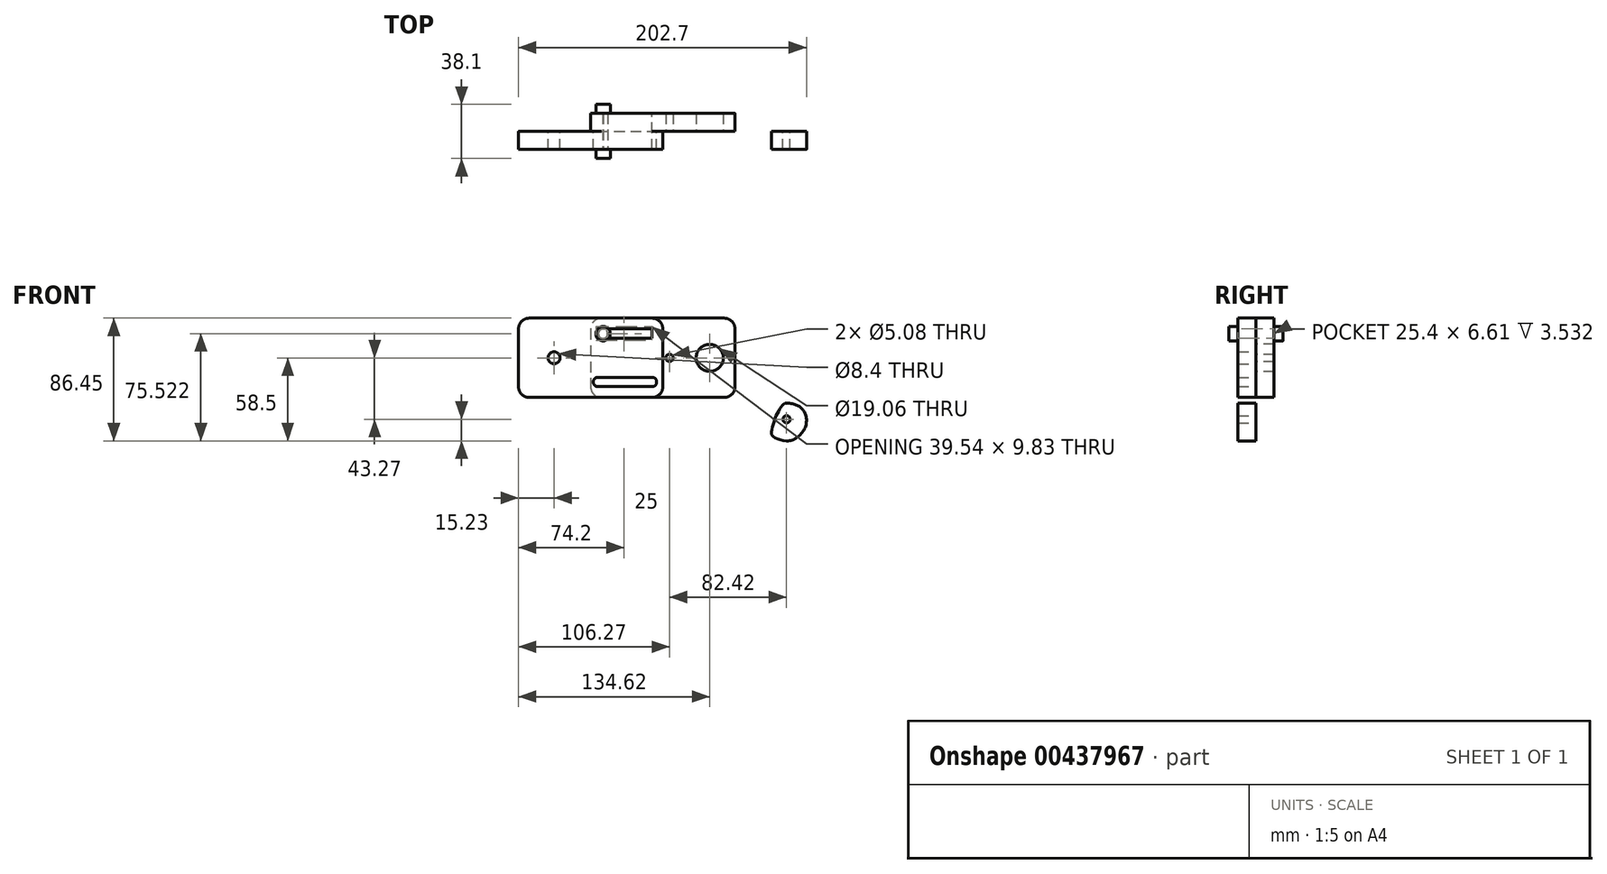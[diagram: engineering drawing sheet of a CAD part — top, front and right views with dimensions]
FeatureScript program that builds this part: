
annotation { "Feature Type Name" : "Feature", "Feature Type Description" : "" }
export const myFeature = defineFeature(function(context is Context, id is Id, definition is map)
    precondition{}
    {
        {
            var Q0;
            Q0=qCreatedBy(makeId("Front.planeOp"),FACE);
            var sketch = newSketch(context, id + "F0", { "sketchPlane" : qUnion([Q0])});
            skLineSegment(sketch, "E0.bottom", {"start": v(-147.55, 96.25) * mm, "end": v(-61.2, 96.25) * mm});
            skLineSegment(sketch, "E0.top", {"start": v(-147.55, 40.37) * mm, "end": v(-61.2, 40.37) * mm});
            skLineSegment(sketch, "E0.left", {"start": v(-155.17, 88.63) * mm, "end": v(-155.17, 47.99) * mm});
            skLineSegment(sketch, "E0.right", {"start": v(-53.57, 88.63) * mm, "end": v(-53.57, 47.99) * mm});
            skCircle(sketch, "E1", {"center": v(-130.17, 68.3) * mm, "radius": 4.2 * mm});
            skPoint(sketch, "E1.centerSnap0", {"position": v(-155.17, 68.3) * mm});
            skLineSegment(sketch, "E2", {"start": v(-99.3, 88.63) * mm, "end": v(-61.2, 88.63) * mm});
            skLineSegment(sketch, "E3", {"start": v(-99.3, 82.02) * mm, "end": v(-61.2, 82.02) * mm});
            skLineSegment(sketch, "E4", {"start": v(-53.57, 68.3) * mm, "end": v(-67.06, 68.3) * mm});
            skArc(sketch, "E5", {"start": v(-99.3, 88.63) * mm, "mid": v(-102.6, 85.32) * mm, "end": v(-99.3, 82.02) * mm});
            skArc(sketch, "E6", {"start": v(-61.2, 82.02) * mm, "mid": v(-57.9, 85.32) * mm, "end": v(-61.2, 88.63) * mm});
            skArc(sketch, "E7.MirrorCS", {"start": v(-99.3, 47.99) * mm, "mid": v(-102.6, 51.29) * mm, "end": v(-99.3, 54.6) * mm});
            skArc(sketch, "E8.MirrorCS", {"start": v(-61.2, 54.6) * mm, "mid": v(-57.9, 51.29) * mm, "end": v(-61.2, 47.99) * mm});
            skLineSegment(sketch, "E9.MirrorCS", {"start": v(-99.3, 54.6) * mm, "end": v(-61.2, 54.6) * mm});
            skLineSegment(sketch, "E10.MirrorCS", {"start": v(-99.3, 47.99) * mm, "end": v(-61.2, 47.99) * mm});
            skPoint(sketch, "E11.visualSharp", {"position": v(-155.17, 96.25) * mm});
            skArc(sketch, "E11.filletArc", {"start": v(-147.55, 96.25) * mm, "mid": v(-152.94, 94.02) * mm, "end": v(-155.17, 88.63) * mm});
            skPoint(sketch, "E12.visualSharp", {"position": v(-155.17, 40.37) * mm});
            skArc(sketch, "E12.filletArc", {"start": v(-155.17, 47.99) * mm, "mid": v(-152.94, 42.6) * mm, "end": v(-147.55, 40.37) * mm});
            skPoint(sketch, "E13.visualSharp", {"position": v(-53.57, 96.25) * mm});
            skArc(sketch, "E13.filletArc", {"start": v(-53.57, 88.63) * mm, "mid": v(-55.8, 94.02) * mm, "end": v(-61.2, 96.25) * mm});
            skPoint(sketch, "E14.visualSharp", {"position": v(-53.57, 40.37) * mm});
            skArc(sketch, "E14.filletArc", {"start": v(-61.2, 40.37) * mm, "mid": v(-55.8, 42.6) * mm, "end": v(-53.57, 47.99) * mm});
            skArc(sketch, "E15", {"start": v(-53.57, 73.39) * mm, "mid": v(-53.99, 68.3) * mm, "end": v(-53.57, 63.23) * mm});
            skCircle(sketch, "E16", {"center": v(-130.17, 68.3) * mm, "radius": 29.6 * mm});
            skLineSegment(sketch, "E17", {"start": v(-99.3, 88.63) * mm, "end": v(-99.3, 82.02) * mm});
            skLineSegment(sketch, "E18", {"start": v(-61.2, 82.02) * mm, "end": v(-61.2, 88.63) * mm});
            skLineSegment(sketch, "E19", {"start": v(-99.3, 54.6) * mm, "end": v(-99.3, 47.99) * mm});
            skLineSegment(sketch, "E20", {"start": v(-61.2, 54.6) * mm, "end": v(-61.2, 47.99) * mm});
            skSolve(sketch);
        }
        {
            var Q0;
            Q0=makeQuery(id+"F0.imprint","IMPRINT",FACE,{"disambiguationData":[TD([[makeQuery(id+"F0.imprint","IMPRINT",EDGE,{"derivedFrom":sQuery(id+"F0.wireOp",EDGE,"E0.left")}),1.0]])]});
            var Q1;
            Q1=makeQuery(id+"F0.imprint","IMPRINT",FACE,{"disambiguationData":[TD([[makeQuery(id+"F0.imprint","IMPRINT",EDGE,{"derivedFrom":sQuery(id+"F0.wireOp",EDGE,"E2")}),1.0]])]});
            var Q2;
            Q2=makeQuery(id+"F0.imprint","IMPRINT",FACE,{"disambiguationData":[TD([[makeQuery(id+"F0.imprint","IMPRINT",EDGE,{"derivedFrom":sQuery(id+"F0.wireOp",EDGE,"E1")}),-1.0]])]});
            var Q3;
            Q3=makeQuery(id+"F0.imprint","IMPRINT",FACE,{"disambiguationData":[TD([[makeQuery(id+"F0.imprint","IMPRINT",EDGE,{"derivedFrom":sQuery(id+"F0.wireOp",EDGE,"E1")}),-1.0]])]});
            var Q4;
            Q4=makeQuery(id+"F0.imprint","IMPRINT",FACE,{"disambiguationData":[TD([[makeQuery(id+"F0.imprint","IMPRINT",EDGE,{"derivedFrom":sQuery(id+"F0.wireOp",EDGE,"E6")}),1.0]])]});
            var Q5;
            Q5=makeQuery(id+"F0.imprint","IMPRINT",FACE,{"disambiguationData":[TD([[makeQuery(id+"F0.imprint","IMPRINT",EDGE,{"derivedFrom":sQuery(id+"F0.wireOp",EDGE,"E5")}),1.0]])]});
            var Q6;
            Q6=makeQuery(id+"F0.imprint","IMPRINT",FACE,{"disambiguationData":[TD([[makeQuery(id+"F0.imprint","IMPRINT",EDGE,{"derivedFrom":sQuery(id+"F0.wireOp",EDGE,"E7.MirrorCS")}),-1.0]])]});
            var Q7;
            Q7=makeQuery(id+"F0.imprint","IMPRINT",FACE,{"disambiguationData":[TD([[makeQuery(id+"F0.imprint","IMPRINT",EDGE,{"derivedFrom":sQuery(id+"F0.wireOp",EDGE,"E8.MirrorCS")}),-1.0]])]});
            var Q8;
            {var subQ0=sQuery(id+"F0.wireOp",EDGE,"E4");var subQ1=sQuery(id+"F0.wireOp",EDGE,"E0.right");var subQ2=makeQuery(id+"F0.imprint","INTERSECT",VERTEX,{"derivedFrom":[subQ1,subQ0]});Q8=makeQuery(id+"F0.imprint","IMPRINT",FACE,{"disambiguationData":[TD([[makeQuery(id+"F0.imprint","IMPRINT",EDGE,{"disambiguationData":[TD([[subQ2,-1.0]])],"derivedFrom":subQ1}),-1.0]])]});}
            var Q9;
            {var subQ0=sQuery(id+"F0.wireOp",EDGE,"E4");var subQ1=sQuery(id+"F0.wireOp",EDGE,"E0.right");var subQ2=makeQuery(id+"F0.imprint","INTERSECT",VERTEX,{"derivedFrom":[subQ1,subQ0]});Q9=makeQuery(id+"F0.imprint","IMPRINT",FACE,{"disambiguationData":[TD([[makeQuery(id+"F0.imprint","IMPRINT",EDGE,{"disambiguationData":[TD([[subQ2,1.0]])],"derivedFrom":subQ1}),-1.0]])]});}
            extrude(context, id + "F1", {"entities" : qUnion([Q0, Q1, Q2, Q3, Q4, Q5, Q6, Q7, Q8, Q9]), "depth" : 12.7 * mm});
        }
        {
            var Q0;
            Q0=makeQuery(id+"F1.opExtrude","CAP_FACE",FACE,{"disambiguationData":[OSD([sQuery(id+"F0.wireOp",EDGE,"E0.bottom"),sQuery(id+"F0.wireOp",EDGE,"E0.top"),sQuery(id+"F0.wireOp",EDGE,"E0.left"),sQuery(id+"F0.wireOp",EDGE,"E0.right"),sQuery(id+"F0.wireOp",EDGE,"E1"),sQuery(id+"F0.wireOp",EDGE,"E2"),sQuery(id+"F0.wireOp",EDGE,"E3"),sQuery(id+"F0.wireOp",EDGE,"E5"),sQuery(id+"F0.wireOp",EDGE,"E6"),sQuery(id+"F0.wireOp",EDGE,"E7.MirrorCS"),sQuery(id+"F0.wireOp",EDGE,"E8.MirrorCS"),sQuery(id+"F0.wireOp",EDGE,"E9.MirrorCS"),sQuery(id+"F0.wireOp",EDGE,"E10.MirrorCS"),sQuery(id+"F0.wireOp",EDGE,"E11.filletArc"),sQuery(id+"F0.wireOp",EDGE,"E12.filletArc")])],"isStart":true});
            var sketch = newSketch(context, id + "F2", { "sketchPlane" : qUnion([Q0])});
            skCircle(sketch, "E21", {"center": v(130.17, 68.3) * mm, "radius": 29.6 * mm});
            skLineSegment(sketch, "E22.bottom", {"start": v(96.75, 96.25) * mm, "end": v(10.4, 96.25) * mm});
            skLineSegment(sketch, "E22.top", {"start": v(96.75, 40.37) * mm, "end": v(10.4, 40.37) * mm});
            skLineSegment(sketch, "E22.left", {"start": v(104.37, 88.63) * mm, "end": v(104.37, 47.99) * mm});
            skLineSegment(sketch, "E22.right", {"start": v(2.77, 88.63) * mm, "end": v(2.77, 47.99) * mm});
            skCircle(sketch, "E23", {"center": v(20.55, 68.3) * mm, "radius": 9.53 * mm});
            skPoint(sketch, "E23.centerSnap0", {"position": v(2.77, 68.3) * mm});
            skArc(sketch, "E24", {"start": v(61.2, 88.63) * mm, "mid": v(57.9, 85.32) * mm, "end": v(61.2, 82.02) * mm});
            skArc(sketch, "E25", {"start": v(98.02, 82.02) * mm, "mid": v(101.33, 85.32) * mm, "end": v(98.02, 88.63) * mm});
            skLineSegment(sketch, "E26", {"start": v(61.2, 88.63) * mm, "end": v(98.02, 88.63) * mm});
            skLineSegment(sketch, "E27", {"start": v(61.2, 82.02) * mm, "end": v(98.02, 82.02) * mm});
            skLineSegment(sketch, "E28", {"start": v(2.77, 68.3) * mm, "end": v(11.81, 68.3) * mm});
            skArc(sketch, "E29.MirrorCS", {"start": v(61.2, 47.99) * mm, "mid": v(57.9, 51.29) * mm, "end": v(61.2, 54.6) * mm});
            skLineSegment(sketch, "E30.MirrorCS", {"start": v(61.2, 54.6) * mm, "end": v(98.02, 54.6) * mm});
            skArc(sketch, "E31.MirrorCS", {"start": v(98.02, 54.6) * mm, "mid": v(101.33, 51.29) * mm, "end": v(98.02, 47.99) * mm});
            skLineSegment(sketch, "E32.MirrorCS", {"start": v(61.2, 47.99) * mm, "end": v(98.02, 47.99) * mm});
            skPoint(sketch, "E33.visualSharp", {"position": v(104.37, 96.25) * mm});
            skArc(sketch, "E33.filletArc", {"start": v(104.37, 88.63) * mm, "mid": v(102.14, 94.02) * mm, "end": v(96.75, 96.25) * mm});
            skPoint(sketch, "E34.visualSharp", {"position": v(104.37, 40.37) * mm});
            skArc(sketch, "E34.filletArc", {"start": v(96.75, 40.37) * mm, "mid": v(102.14, 42.6) * mm, "end": v(104.37, 47.99) * mm});
            skPoint(sketch, "E35.visualSharp", {"position": v(2.77, 96.25) * mm});
            skArc(sketch, "E35.filletArc", {"start": v(10.4, 96.25) * mm, "mid": v(5, 94.02) * mm, "end": v(2.77, 88.63) * mm});
            skPoint(sketch, "E36.visualSharp", {"position": v(2.77, 40.37) * mm});
            skArc(sketch, "E36.filletArc", {"start": v(2.77, 47.99) * mm, "mid": v(5, 42.6) * mm, "end": v(10.4, 40.37) * mm});
            skCircle(sketch, "E37", {"center": v(48.9, 68.3) * mm, "radius": 2.54 * mm});
            skSolve(sketch);
        }
        {
            var Q0;
            Q0=makeQuery(id+"F2.imprint","IMPRINT",FACE,{"disambiguationData":[TD([[makeQuery(id+"F2.imprint","IMPRINT",EDGE,{"derivedFrom":sQuery(id+"F2.wireOp",EDGE,"E23")}),-1.0]])]});
            var Q1;
            Q1=makeQuery(id+"F2.imprint","IMPRINT",FACE,{"disambiguationData":[TD([[makeQuery(id+"F2.imprint","IMPRINT",EDGE,{"derivedFrom":sQuery(id+"F2.wireOp",EDGE,"E24")}),1.0]])]});
            var Q2;
            {var subQ0=sQuery(id+"F2.wireOp",EDGE,"E22.left");var subQ1=sQuery(id+"F2.wireOp",EDGE,"E21");var subQ2=makeQuery(id+"F2.imprint","INTERSECT",VERTEX,{"disambiguationData":[OD(0.0)],"derivedFrom":[subQ1,subQ0]});Q2=makeQuery(id+"F2.imprint","IMPRINT",FACE,{"disambiguationData":[TD([[makeQuery(id+"F2.imprint","IMPRINT",EDGE,{"disambiguationData":[TD([[subQ2,-1.0]])],"derivedFrom":subQ1}),1.0]])]});}
            var Q3;
            Q3=makeQuery(id+"F2.imprint","IMPRINT",FACE,{"disambiguationData":[TD([[makeQuery(id+"F2.imprint","IMPRINT",EDGE,{"derivedFrom":sQuery(id+"F2.wireOp",EDGE,"E24")}),-1.0]])]});
            var Q4;
            {var subQ0=sQuery(id+"F2.wireOp",EDGE,"E25");var subQ1=makeQuery(id+"F1.opExtrude","CAP_EDGE",EDGE,{"disambiguationData":[OSD([sQuery(id+"F0.wireOp",EDGE,"E17")])],"isStart":true});var subQ2=makeQuery(id+"F2.imprint","INTERSECT",VERTEX,{"disambiguationData":[OD(0.0)],"derivedFrom":[subQ1,subQ0]});Q4=makeQuery(id+"F2.imprint","IMPRINT",FACE,{"disambiguationData":[TD([[makeQuery(id+"F2.imprint","IMPRINT",EDGE,{"disambiguationData":[TD([[subQ2,-1.0]])],"derivedFrom":subQ0}),1.0]])]});}
            var Q5;
            {var subQ0=sQuery(id+"F2.wireOp",EDGE,"E31.MirrorCS");var subQ1=makeQuery(id+"F1.opExtrude","CAP_EDGE",EDGE,{"disambiguationData":[OSD([sQuery(id+"F0.wireOp",EDGE,"E19")])],"isStart":true});var subQ2=makeQuery(id+"F2.imprint","INTERSECT",VERTEX,{"disambiguationData":[OD(0.0)],"derivedFrom":[subQ1,subQ0]});Q5=makeQuery(id+"F2.imprint","IMPRINT",FACE,{"disambiguationData":[TD([[makeQuery(id+"F2.imprint","IMPRINT",EDGE,{"disambiguationData":[TD([[subQ2,-1.0]])],"derivedFrom":subQ0}),-1.0]])]});}
            var Q6;
            Q6=makeQuery(id+"F2.imprint","IMPRINT",FACE,{"disambiguationData":[TD([[makeQuery(id+"F2.imprint","IMPRINT",EDGE,{"derivedFrom":sQuery(id+"F2.wireOp",EDGE,"E29.MirrorCS")}),-1.0]])]});
            extrude(context, id + "F3", {"entities" : qUnion([Q0, Q1, Q2, Q3, Q4, Q5, Q6]), "depth" : 12.7 * mm});
        }
        {
            var Q0;
            Q0=makeQuery(id+"F3.opExtrude","CAP_FACE",FACE,{"disambiguationData":[OSD([sQuery(id+"F0.wireOp",EDGE,"E2"),sQuery(id+"F0.wireOp",EDGE,"E3"),sQuery(id+"F0.wireOp",EDGE,"E5"),sQuery(id+"F0.wireOp",EDGE,"E7.MirrorCS"),sQuery(id+"F0.wireOp",EDGE,"E9.MirrorCS"),sQuery(id+"F0.wireOp",EDGE,"E10.MirrorCS"),sQuery(id+"F2.wireOp",EDGE,"E22.bottom"),sQuery(id+"F2.wireOp",EDGE,"E22.top"),sQuery(id+"F2.wireOp",EDGE,"E22.left"),sQuery(id+"F2.wireOp",EDGE,"E22.right"),sQuery(id+"F2.wireOp",EDGE,"E23"),sQuery(id+"F2.wireOp",EDGE,"E24"),sQuery(id+"F2.wireOp",EDGE,"E26"),sQuery(id+"F2.wireOp",EDGE,"E27"),sQuery(id+"F2.wireOp",EDGE,"E29.MirrorCS"),sQuery(id+"F2.wireOp",EDGE,"E30.MirrorCS"),sQuery(id+"F2.wireOp",EDGE,"E32.MirrorCS"),sQuery(id+"F2.wireOp",EDGE,"E33.filletArc"),sQuery(id+"F2.wireOp",EDGE,"E34.filletArc"),sQuery(id+"F2.wireOp",EDGE,"E35.filletArc"),sQuery(id+"F2.wireOp",EDGE,"E36.filletArc"),sQuery(id+"F2.wireOp",EDGE,"E37")])],"isStart":true});
            var sketch = newSketch(context, id + "F4", { "sketchPlane" : qUnion([Q0])});
            skLineSegment(sketch, "E38", {"start": v(-48.9, 68.3) * mm, "end": v(-48.9, 79.74) * mm});
            skLineSegment(sketch, "E39", {"start": v(-48.9, 68.3) * mm, "end": v(-34.94, 68.3) * mm});
            skLineSegment(sketch, "E40", {"start": v(-48.9, 68.3) * mm, "end": v(-48.9, 53.07) * mm});
            skFitSpline(sketch, "E41", {"points": [v(-60.03, 57.89) * mm, v(-56.51, 55.58) * mm, v(-48.9, 53.07) * mm, v(-41.82, 55.25) * mm, v(-36.46, 61.17) * mm, v(-34.94, 68.3) * mm, v(-37.37, 74.98) * mm, v(-42.74, 78.67) * mm, v(-48.9, 79.74) * mm], "startDerivative": vector(31.94, -23.59) * mm, "endDerivative": vector(-54.54, 0.34) * mm});
            skFitSpline(sketch, "E42", {"points": [v(-48.9, 79.74) * mm, v(-50.92, 79.03) * mm, v(-53.27, 68.6) * mm, v(-57.4, 60.89) * mm, v(-59.1, 59.85) * mm, v(-59.61, 58.56) * mm, v(-58.83, 57.02) * mm], "startDerivative": vector(-17.65, -0.32) * mm, "endDerivative": vector(9.72, -13.34) * mm});
            skLineSegment(sketch, "E43", {"start": v(33.52, 25.03) * mm, "end": v(33.52, 36.46) * mm});
            skLineSegment(sketch, "E44", {"start": v(33.52, 25.03) * mm, "end": v(47.5, 25.03) * mm});
            skLineSegment(sketch, "E45", {"start": v(33.52, 25.03) * mm, "end": v(33.52, 9.8) * mm});
            skFitSpline(sketch, "E46", {"points": [v(33.52, 36.46) * mm, v(39.7, 35.4) * mm, v(45.06, 31.71) * mm, v(47.5, 25.03) * mm, v(45.97, 17.9) * mm, v(40.6, 11.97) * mm, v(33.52, 9.8) * mm, v(25.21, 12.12) * mm, v(23.23, 13.91) * mm, v(22.82, 15.29) * mm, v(23.4, 18.83) * mm, v(25.9, 26.7) * mm, v(28.8, 32.3) * mm, v(31.51, 35.75) * mm, v(33.52, 36.46) * mm]});
            skCircle(sketch, "E47", {"center": v(33.52, 25.03) * mm, "radius": 2.54 * mm});
            skSolve(sketch);
        }
        {
            var Q0;
            {var subQ0=sQuery(id+"F4.wireOp",EDGE,"1zBz8o6W-lrHy-W7YF-fYqX-U7H7Ej3Si0ow");var subQ1=sQuery(id+"F4.wireOp",EDGE,"a7affe35-fed5-418f-ad31-c611f1f3193c");var subQ2=makeQuery(id+"F4.imprint","INTERSECT",VERTEX,{"disambiguationData":[OD(0.0)],"derivedFrom":[subQ1,subQ0]});Q0=makeQuery(id+"F4.imprint","IMPRINT",FACE,{"disambiguationData":[TD([[makeQuery(id+"F4.imprint","IMPRINT",EDGE,{"disambiguationData":[TD([[subQ2,-1.0]])],"derivedFrom":subQ1}),1.0]])]});}
            var Q1;
            {var subQ0=sQuery(id+"F4.wireOp",EDGE,"E41");var subQ1=sQuery(id+"F4.wireOp",EDGE,"E39");var subQ2=makeQuery(id+"F4.imprint","INTERSECT",VERTEX,{"derivedFrom":[subQ1,subQ0]});Q1=makeQuery(id+"F4.imprint","IMPRINT",FACE,{"disambiguationData":[TD([[makeQuery(id+"F4.imprint","IMPRINT",EDGE,{"disambiguationData":[TD([[subQ2,1.0]])],"derivedFrom":subQ1}),-1.0]])]});}
            var Q2;
            {var subQ3=sQuery(id+"F4.wireOp",EDGE,"C4wERMpf-pKPf-LVwF-GBsw-geDMRwuV3cjk");Q2=makeQuery(id+"F4.imprint","IMPRINT",FACE,{"disambiguationData":[TD([[makeQuery(id+"F4.imprint","IMPRINT",EDGE,{"derivedFrom":subQ3}),1.0]])]});}
            var Q3;
            {var subQ0=sQuery(id+"F4.wireOp",EDGE,"E41");var subQ5=sQuery(id+"F4.wireOp",EDGE,"E39");var subQ7=makeQuery(id+"F4.imprint","INTERSECT",VERTEX,{"derivedFrom":[subQ5,subQ0]});Q3=makeQuery(id+"F4.imprint","IMPRINT",FACE,{"disambiguationData":[TD([[makeQuery(id+"F4.imprint","IMPRINT",EDGE,{"disambiguationData":[TD([[subQ7,1.0]])],"derivedFrom":subQ5}),1.0]])]});}
            var Q4;
            {var subQ0=sQuery(id+"F4.wireOp",EDGE,"E42");Q4=makeQuery(id+"F4.imprint","IMPRINT",FACE,{"disambiguationData":[TD([[makeQuery(id+"F4.imprint","IMPRINT",EDGE,{"derivedFrom":subQ0}),1.0]])]});}
            var Q5;
            {var subQ0=sQuery(id+"F4.wireOp",EDGE,"E46");var subQ1=sQuery(id+"F4.wireOp",EDGE,"E43");var subQ2=makeQuery(id+"F4.imprint","INTERSECT",VERTEX,{"derivedFrom":[subQ1,subQ0]});Q5=makeQuery(id+"F4.imprint","IMPRINT",FACE,{"disambiguationData":[TD([[makeQuery(id+"F4.imprint","IMPRINT",EDGE,{"disambiguationData":[TD([[subQ2,1.0]])],"derivedFrom":subQ1}),1.0]])]});}
            var Q6;
            {var subQ0=sQuery(id+"F4.wireOp",EDGE,"E46");var subQ1=sQuery(id+"F4.wireOp",EDGE,"E44");var subQ2=makeQuery(id+"F4.imprint","INTERSECT",VERTEX,{"derivedFrom":[subQ1,subQ0]});Q6=makeQuery(id+"F4.imprint","IMPRINT",FACE,{"disambiguationData":[TD([[makeQuery(id+"F4.imprint","IMPRINT",EDGE,{"disambiguationData":[TD([[subQ2,1.0]])],"derivedFrom":subQ1}),-1.0]])]});}
            var Q7;
            {var subQ0=sQuery(id+"F4.wireOp",EDGE,"E46");var subQ1=sQuery(id+"F4.wireOp",EDGE,"E43");var subQ2=makeQuery(id+"F4.imprint","INTERSECT",VERTEX,{"derivedFrom":[subQ1,subQ0]});Q7=makeQuery(id+"F4.imprint","IMPRINT",FACE,{"disambiguationData":[TD([[makeQuery(id+"F4.imprint","IMPRINT",EDGE,{"disambiguationData":[TD([[subQ2,1.0]])],"derivedFrom":subQ1}),-1.0]])]});}
            extrude(context, id + "F5", {"entities" : qUnion([Q0, Q1, Q2, Q3, Q4, Q5, Q6, Q7]), "depth" : 12.7 * mm});
        }
        {
            var Q0;
            Q0=makeQuery(id+"F1.opExtrude","CAP_FACE",FACE,{"disambiguationData":[OSD([sQuery(id+"F0.wireOp",EDGE,"E0.bottom"),sQuery(id+"F0.wireOp",EDGE,"E0.top"),sQuery(id+"F0.wireOp",EDGE,"E0.left"),sQuery(id+"F0.wireOp",EDGE,"E0.right"),sQuery(id+"F0.wireOp",EDGE,"E1"),sQuery(id+"F0.wireOp",EDGE,"E2"),sQuery(id+"F0.wireOp",EDGE,"E3"),sQuery(id+"F0.wireOp",EDGE,"E9.MirrorCS"),sQuery(id+"F0.wireOp",EDGE,"E10.MirrorCS"),sQuery(id+"F0.wireOp",EDGE,"E11.filletArc"),sQuery(id+"F0.wireOp",EDGE,"E12.filletArc"),sQuery(id+"F0.wireOp",EDGE,"E13.filletArc"),sQuery(id+"F0.wireOp",EDGE,"E14.filletArc"),sQuery(id+"F0.wireOp",EDGE,"E17"),sQuery(id+"F0.wireOp",EDGE,"E18"),sQuery(id+"F0.wireOp",EDGE,"E19"),sQuery(id+"F0.wireOp",EDGE,"E20")])],"isStart":false});
            var sketch = newSketch(context, id + "F6", { "sketchPlane" : qUnion([Q0])});
            skArc(sketch, "E48", {"start": v(-98.86, 84.5) * mm, "mid": v(-92.36, 85.32) * mm, "end": v(-98.86, 86.14) * mm});
            skPoint(sketch, "E48.centerSnap0", {"position": v(-99.3, 85.32) * mm});
            skLineSegment(sketch, "E49", {"start": v(-98.86, 84.5) * mm, "end": v(-98.86, 86.14) * mm});
            skSolve(sketch);
        }
        {
            var Q0;
            Q0=qSketchRegion(id+"F6",true);
            extrude(context, id + "F7", {"entities" : qUnion([Q0]), "oppositeDirection" : true, "depth" : 25.4 * mm});
        }
        {
            var Q0;
            Q0=makeQuery(id+"F7.opExtrude","CAP_FACE",FACE,{"disambiguationData":[OSD([sQuery(id+"F6.wireOp",EDGE,"E48"),sQuery(id+"F6.wireOp",EDGE,"E49")])],"isStart":true});
            var sketch = newSketch(context, id + "F8", { "sketchPlane" : qUnion([Q0])});
            skCircle(sketch, "E50", {"center": v(-95.66, 85.32) * mm, "radius": 5.08 * mm});
            skSolve(sketch);
        }
        {
            var Q0;
            Q0=qSketchRegion(id+"F8",true);
            extrude(context, id + "F9", {"entities" : qUnion([Q0]), "operationType" : NewBodyOperationType.ADD, "depth" : 6.35 * mm});
        }
        {
            var Q0;
            Q0=makeQuery(id+"F5.opExtrude","SWEPT_BODY",BODY,{"disambiguationData":[OSD([sQuery(id+"F2.wireOp",EDGE,"E37"),sQuery(id+"F4.wireOp",EDGE,"E41"),sQuery(id+"F4.wireOp",EDGE,"E42")])]});
            deleteBodies(context, id + "F10", {"entities" : qUnion([Q0])});
        }
        {
            var Q0;
            Q0=makeQuery(id+"F7.opExtrude","CAP_FACE",FACE,{"disambiguationData":[OSD([sQuery(id+"F6.wireOp",EDGE,"E48"),sQuery(id+"F6.wireOp",EDGE,"E49")])],"isStart":false});
            var sketch = newSketch(context, id + "F11", { "sketchPlane" : qUnion([Q0])});
            skCircle(sketch, "E51", {"center": v(95.66, 85.32) * mm, "radius": 5.08 * mm});
            skSolve(sketch);
        }
        {
            var Q0;
            Q0=qSketchRegion(id+"F11",true);
            extrude(context, id + "F12", {"entities" : qUnion([Q0]), "operationType" : NewBodyOperationType.ADD, "depth" : 6.35 * mm});
        }
    });
